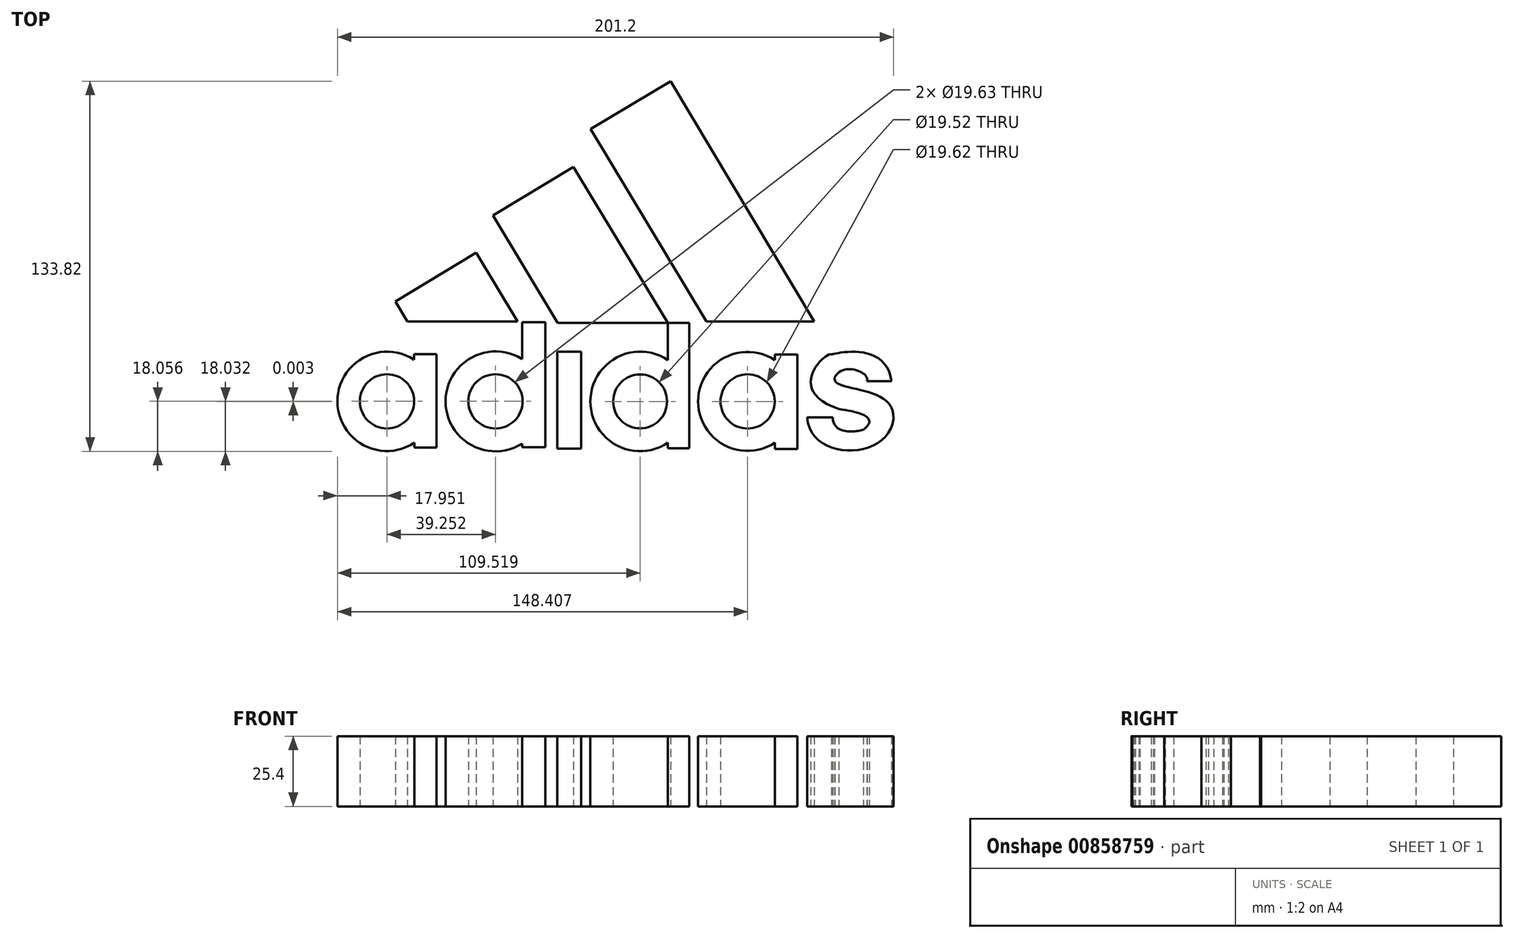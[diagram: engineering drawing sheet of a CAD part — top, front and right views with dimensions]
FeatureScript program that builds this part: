
annotation { "Feature Type Name" : "Feature", "Feature Type Description" : "" }
export const myFeature = defineFeature(function(context is Context, id is Id, definition is map)
    precondition{}
    {
        {
            var Q0;
            Q0=qCreatedBy(makeId("Top.planeOp"),FACE);
            var sketch = newSketch(context, id + "F0", { "sketchPlane" : qUnion([Q0])});
            skLineSegment(sketch, "E0", {"start": v(-79.35, -22.5) * mm, "end": v(-74.98, -29.75) * mm});
            skLineSegment(sketch, "E1", {"start": v(-74.27, -29.75) * mm, "end": v(-35.08, -29.75) * mm});
            skLineSegment(sketch, "E2", {"start": v(-74.98, -29.75) * mm, "end": v(-73.76, -29.75) * mm});
            skLineSegment(sketch, "E3", {"start": v(-79.35, -22.5) * mm, "end": v(-50.12, -4.9) * mm});
            skLineSegment(sketch, "E4", {"start": v(-50.12, -4.9) * mm, "end": v(-35.08, -29.75) * mm});
            skLineSegment(sketch, "E5", {"start": v(-44, 8.56) * mm, "end": v(-14.9, 26.17) * mm});
            skLineSegment(sketch, "E6", {"start": v(-14.9, 26.17) * mm, "end": v(19.24, -30.26) * mm});
            skLineSegment(sketch, "E7", {"start": v(19.24, -30.26) * mm, "end": v(-20.64, -30.26) * mm});
            skLineSegment(sketch, "E8", {"start": v(-20.64, -30.26) * mm, "end": v(-44, 8.56) * mm});
            skLineSegment(sketch, "E9", {"start": v(-8.7, 39.76) * mm, "end": v(20.28, 57.1) * mm});
            skLineSegment(sketch, "E10", {"start": v(20.28, 57.1) * mm, "end": v(72.27, -29.77) * mm});
            skLineSegment(sketch, "E11", {"start": v(72.27, -29.77) * mm, "end": v(33.24, -29.77) * mm});
            skLineSegment(sketch, "E12", {"start": v(33.24, -29.77) * mm, "end": v(-8.7, 39.76) * mm});
            skCircle(sketch, "E13", {"center": v(-82.34, -58.65) * mm, "radius": 9.82 * mm});
            skCircle(sketch, "E14", {"center": v(-82.34, -58.65) * mm, "radius": 17.95 * mm});
            skLineSegment(sketch, "E15", {"start": v(-72.58, -41.59) * mm, "end": v(-64.44, -41.59) * mm});
            skLineSegment(sketch, "E16", {"start": v(-64.44, -41.59) * mm, "end": v(-64.44, -75.34) * mm});
            skLineSegment(sketch, "E17", {"start": v(-64.44, -75.34) * mm, "end": v(-72.4, -75.34) * mm});
            skLineSegment(sketch, "E18", {"start": v(-72.4, -75.34) * mm, "end": v(-72.4, -73.6) * mm});
            skLineSegment(sketch, "E19", {"start": v(-72.58, -41.59) * mm, "end": v(-72.58, -43.59) * mm});
            skCircle(sketch, "E20", {"center": v(-43.09, -58.65) * mm, "radius": 9.81 * mm});
            skLineSegment(sketch, "E21.bottom", {"start": v(-33.5, -30.01) * mm, "end": v(-25.1, -30.01) * mm});
            skLineSegment(sketch, "E21.top", {"start": v(-33.5, -75.26) * mm, "end": v(-25.1, -75.26) * mm});
            skLineSegment(sketch, "E21.left", {"start": v(-33.5, -30.01) * mm, "end": v(-33.5, -75.26) * mm});
            skLineSegment(sketch, "E21.right", {"start": v(-25.1, -30.01) * mm, "end": v(-25.1, -75.26) * mm});
            skCircle(sketch, "E22", {"center": v(-43.09, -58.65) * mm, "radius": 18.06 * mm});
            skLineSegment(sketch, "E23.bottom", {"start": v(-20.8, -40.66) * mm, "end": v(-12.17, -40.66) * mm});
            skLineSegment(sketch, "E23.top", {"start": v(-20.8, -75.79) * mm, "end": v(-12.17, -75.79) * mm});
            skLineSegment(sketch, "E23.left", {"start": v(-20.8, -40.66) * mm, "end": v(-20.8, -75.79) * mm});
            skLineSegment(sketch, "E23.right", {"start": v(-12.17, -40.66) * mm, "end": v(-12.17, -75.79) * mm});
            skLineSegment(sketch, "E24.bottom", {"start": v(-20.64, -30.26) * mm, "end": v(-12.17, -30.26) * mm});
            skLineSegment(sketch, "E24.top", {"start": v(-20.64, -38.2) * mm, "end": v(-12.17, -38.2) * mm});
            skLineSegment(sketch, "E24.left", {"start": v(-20.64, -30.26) * mm, "end": v(-20.64, -38.2) * mm});
            skLineSegment(sketch, "E24.right", {"start": v(-12.17, -30.26) * mm, "end": v(-12.17, -38.2) * mm});
            skCircle(sketch, "E25", {"center": v(9.23, -58.68) * mm, "radius": 9.76 * mm});
            skCircle(sketch, "E26", {"center": v(9.23, -58.68) * mm, "radius": 18 * mm});
            skLineSegment(sketch, "E27.bottom", {"start": v(19.24, -30.26) * mm, "end": v(27, -30.26) * mm});
            skLineSegment(sketch, "E27.top", {"start": v(19.24, -75.57) * mm, "end": v(27, -75.57) * mm});
            skLineSegment(sketch, "E27.left", {"start": v(19.24, -30.26) * mm, "end": v(19.24, -75.57) * mm});
            skLineSegment(sketch, "E27.right", {"start": v(27, -30.26) * mm, "end": v(27, -75.57) * mm});
            skCircle(sketch, "E28", {"center": v(48.12, -58.68) * mm, "radius": 9.81 * mm});
            skCircle(sketch, "E29", {"center": v(48.12, -58.68) * mm, "radius": 17.9 * mm});
            skLineSegment(sketch, "E30.bottom", {"start": v(58, -41.66) * mm, "end": v(66.1, -41.66) * mm});
            skLineSegment(sketch, "E30.top", {"start": v(58, -75.83) * mm, "end": v(66.1, -75.83) * mm});
            skLineSegment(sketch, "E30.left", {"start": v(58, -41.66) * mm, "end": v(58, -75.83) * mm});
            skLineSegment(sketch, "E30.right", {"start": v(66.1, -41.66) * mm, "end": v(66.1, -75.83) * mm});
            skFitSpline(sketch, "E31", {"points": [v(69.66, -64.45) * mm, v(100.9, -64.9) * mm], "startDerivative": vector(3.19, -48.5) * mm, "endDerivative": vector(4.3, 45.53) * mm});
            skFitSpline(sketch, "E32", {"points": [v(100.9, -64.9) * mm, v(79.73, -49.74) * mm], "startDerivative": vector(1.77, 39.22) * mm, "endDerivative": vector(7.34, 18.34) * mm});
            skFitSpline(sketch, "E33", {"points": [v(79.73, -49.74) * mm, v(91.25, -51.37) * mm], "startDerivative": vector(9.55, 16.05) * mm, "endDerivative": vector(-3.83, -9.95) * mm});
            skLineSegment(sketch, "E34", {"start": v(100.17, -51.4) * mm, "end": v(91.25, -51.37) * mm});
            skFitSpline(sketch, "E35", {"points": [v(81.14, -61.43) * mm, v(89.98, -68.83) * mm], "startDerivative": vector(28.57, -3.62) * mm, "endDerivative": vector(-15.4, -11.23) * mm});
            skFitSpline(sketch, "E36", {"points": [v(89.98, -68.83) * mm, v(78.9, -64.45) * mm], "startDerivative": vector(-9.59, -3.5) * mm, "endDerivative": vector(-0.2, 18.21) * mm});
            skFitSpline(sketch, "E37", {"points": [v(100.17, -51.4) * mm, v(78.58, -41.66) * mm, v(78.45, -41.66) * mm], "startDerivative": vector(-6.32, 48.08) * mm, "endDerivative": vector(-5.63, 0) * mm});
            skFitSpline(sketch, "E38", {"points": [v(78.45, -41.66) * mm, v(81.14, -61.43) * mm], "startDerivative": vector(-7.36, 2.37) * mm, "endDerivative": vector(59.21, -19.84) * mm});
            skLineSegment(sketch, "E39", {"start": v(69.66, -64.45) * mm, "end": v(78.9, -64.45) * mm});
            skSolve(sketch);
        }
        {
            var Q0;
            Q0=makeQuery(id+"F0.imprint","IMPRINT",FACE,{"disambiguationData":[TD([[makeQuery(id+"F0.imprint","IMPRINT",EDGE,{"derivedFrom":sQuery(id+"F0.wireOp",EDGE,"E13")}),-1.0]])]});
            var Q1;
            {var subQ4=sQuery(id+"F0.wireOp",EDGE,"E15");Q1=makeQuery(id+"F0.imprint","IMPRINT",FACE,{"disambiguationData":[TD([[makeQuery(id+"F0.imprint","IMPRINT",EDGE,{"derivedFrom":subQ4}),-1.0]])]});}
            var Q2;
            {var subQ4=sQuery(id+"F0.wireOp",EDGE,"E17");Q2=makeQuery(id+"F0.imprint","IMPRINT",FACE,{"disambiguationData":[TD([[makeQuery(id+"F0.imprint","IMPRINT",EDGE,{"derivedFrom":subQ4}),-1.0]])]});}
            var Q3;
            {var subQ0=sQuery(id+"F0.wireOp",EDGE,"E21.left");var subQ1=sQuery(id+"F0.wireOp",EDGE,"E20");var subQ2=makeQuery(id+"F0.imprint","INTERSECT",VERTEX,{"disambiguationData":[OD(0.0)],"derivedFrom":[subQ1,subQ0]});Q3=makeQuery(id+"F0.imprint","IMPRINT",FACE,{"disambiguationData":[TD([[makeQuery(id+"F0.imprint","IMPRINT",EDGE,{"disambiguationData":[TD([[subQ2,-1.0]])],"derivedFrom":subQ1}),-1.0]])]});}
            var Q4;
            {var subQ1=sQuery(id+"F0.wireOp",EDGE,"E21.left");var subQ3=sQuery(id+"F0.wireOp",EDGE,"E20");var subQ9=makeQuery(id+"F0.imprint","INTERSECT",VERTEX,{"disambiguationData":[OD(0.0)],"derivedFrom":[subQ3,subQ1]});Q4=makeQuery(id+"F0.imprint","IMPRINT",FACE,{"disambiguationData":[TD([[makeQuery(id+"F0.imprint","IMPRINT",EDGE,{"disambiguationData":[TD([[subQ9,1.0]])],"derivedFrom":subQ3}),-1.0]])]});}
            var Q5;
            {var subQ0=sQuery(id+"F0.wireOp",EDGE,"E21.bottom");Q5=makeQuery(id+"F0.imprint","IMPRINT",FACE,{"disambiguationData":[TD([[makeQuery(id+"F0.imprint","IMPRINT",EDGE,{"derivedFrom":subQ0}),-1.0]])]});}
            var Q6;
            {var subQ0=sQuery(id+"F0.wireOp",EDGE,"E21.top");Q6=makeQuery(id+"F0.imprint","IMPRINT",FACE,{"disambiguationData":[TD([[makeQuery(id+"F0.imprint","IMPRINT",EDGE,{"derivedFrom":subQ0}),1.0]])]});}
            var Q7;
            Q7=makeQuery(id+"F0.imprint","IMPRINT",FACE,{"disambiguationData":[TD([[makeQuery(id+"F0.imprint","IMPRINT",EDGE,{"derivedFrom":sQuery(id+"F0.wireOp",EDGE,"E23.bottom")}),-1.0]])]});
            var Q8;
            Q8=makeQuery(id+"F0.imprint","IMPRINT",FACE,{"disambiguationData":[TD([[makeQuery(id+"F0.imprint","IMPRINT",EDGE,{"derivedFrom":sQuery(id+"F0.wireOp",EDGE,"E24.bottom")}),-1.0]])]});
            var Q9;
            Q9=makeQuery(id+"F0.imprint","IMPRINT",FACE,{"disambiguationData":[TD([[makeQuery(id+"F0.imprint","IMPRINT",EDGE,{"derivedFrom":sQuery(id+"F0.wireOp",EDGE,"E25")}),-1.0]])]});
            var Q10;
            {var subQ0=sQuery(id+"F0.wireOp",EDGE,"E27.left");var subQ1=sQuery(id+"F0.wireOp",EDGE,"E26");var subQ2=makeQuery(id+"F0.imprint","INTERSECT",VERTEX,{"disambiguationData":[OD(0.0)],"derivedFrom":[subQ1,subQ0]});Q10=makeQuery(id+"F0.imprint","IMPRINT",FACE,{"disambiguationData":[TD([[makeQuery(id+"F0.imprint","IMPRINT",EDGE,{"disambiguationData":[TD([[subQ2,1.0]])],"derivedFrom":subQ1}),1.0]])]});}
            var Q11;
            {var subQ5=sQuery(id+"F0.wireOp",EDGE,"E27.bottom");Q11=makeQuery(id+"F0.imprint","IMPRINT",FACE,{"disambiguationData":[TD([[makeQuery(id+"F0.imprint","IMPRINT",EDGE,{"derivedFrom":subQ5}),-1.0]])]});}
            var Q12;
            {var subQ5=sQuery(id+"F0.wireOp",EDGE,"E27.top");Q12=makeQuery(id+"F0.imprint","IMPRINT",FACE,{"disambiguationData":[TD([[makeQuery(id+"F0.imprint","IMPRINT",EDGE,{"derivedFrom":subQ5}),1.0]])]});}
            var Q13;
            Q13=makeQuery(id+"F0.imprint","IMPRINT",FACE,{"disambiguationData":[TD([[makeQuery(id+"F0.imprint","IMPRINT",EDGE,{"derivedFrom":sQuery(id+"F0.wireOp",EDGE,"E28")}),-1.0]])]});
            var Q14;
            {var subQ0=sQuery(id+"F0.wireOp",EDGE,"E30.left");var subQ1=sQuery(id+"F0.wireOp",EDGE,"E29");var subQ2=makeQuery(id+"F0.imprint","INTERSECT",VERTEX,{"disambiguationData":[OD(0.0)],"derivedFrom":[subQ1,subQ0]});Q14=makeQuery(id+"F0.imprint","IMPRINT",FACE,{"disambiguationData":[TD([[makeQuery(id+"F0.imprint","IMPRINT",EDGE,{"disambiguationData":[TD([[subQ2,1.0]])],"derivedFrom":subQ1}),1.0]])]});}
            var Q15;
            {var subQ1=sQuery(id+"F0.wireOp",EDGE,"E30.bottom");Q15=makeQuery(id+"F0.imprint","IMPRINT",FACE,{"disambiguationData":[TD([[makeQuery(id+"F0.imprint","IMPRINT",EDGE,{"derivedFrom":subQ1}),-1.0]])]});}
            var Q16;
            Q16=makeQuery(id+"F0.imprint","IMPRINT",FACE,{"disambiguationData":[TD([[makeQuery(id+"F0.imprint","IMPRINT",EDGE,{"derivedFrom":sQuery(id+"F0.wireOp",EDGE,"E31")}),1.0]])]});
            var Q17;
            Q17=makeQuery(id+"F0.imprint","IMPRINT",FACE,{"disambiguationData":[TD([[makeQuery(id+"F0.imprint","IMPRINT",EDGE,{"derivedFrom":sQuery(id+"F0.wireOp",EDGE,"E9")}),-1.0]])]});
            var Q18;
            Q18=makeQuery(id+"F0.imprint","IMPRINT",FACE,{"disambiguationData":[TD([[makeQuery(id+"F0.imprint","IMPRINT",EDGE,{"derivedFrom":sQuery(id+"F0.wireOp",EDGE,"E5")}),-1.0]])]});
            var Q19;
            {var subQ3=sQuery(id+"F0.wireOp",EDGE,"E0");Q19=makeQuery(id+"F0.imprint","IMPRINT",FACE,{"disambiguationData":[TD([[makeQuery(id+"F0.imprint","IMPRINT",EDGE,{"derivedFrom":subQ3}),1.0]])]});}
            extrude(context, id + "F1", {"entities" : qUnion([Q0, Q1, Q2, Q3, Q4, Q5, Q6, Q7, Q8, Q9, Q10, Q11, Q12, Q13, Q14, Q15, Q16, Q17, Q18, Q19]), "depth" : 25.4 * mm, "offsetDistance" : 25.4 * mm});
        }
    });
